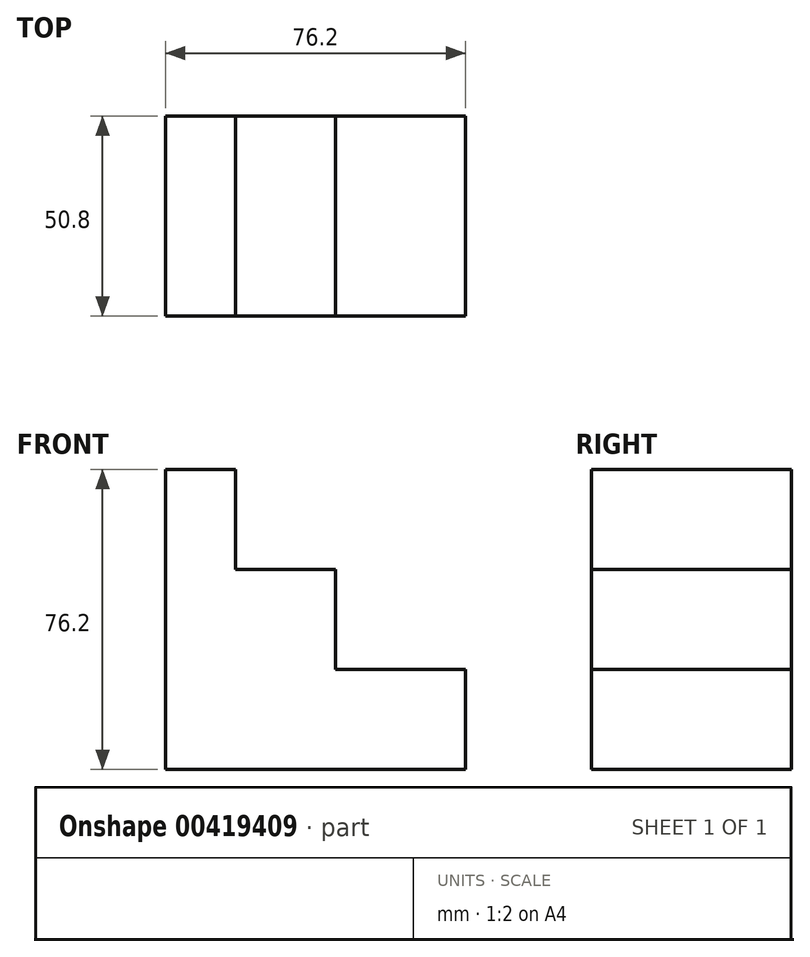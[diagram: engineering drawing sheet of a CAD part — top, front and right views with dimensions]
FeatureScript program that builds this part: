
annotation { "Feature Type Name" : "Feature", "Feature Type Description" : "" }
export const myFeature = defineFeature(function(context is Context, id is Id, definition is map)
    precondition{}
    {
        {
            var Q0;
            Q0=qCreatedBy(makeId("Front.planeOp"),FACE);
            var sketch = newSketch(context, id + "F0", { "sketchPlane" : qUnion([Q0])});
            skLineSegment(sketch, "E0", {"start": v(0, 0) * mm, "end": v(-76.2, 0) * mm});
            skLineSegment(sketch, "E1", {"start": v(-76.2, 0) * mm, "end": v(-76.2, 76.2) * mm});
            skLineSegment(sketch, "E2", {"start": v(-76.2, 76.2) * mm, "end": v(-58.4, 76.2) * mm});
            skLineSegment(sketch, "E3", {"start": v(-58.4, 76.2) * mm, "end": v(-58.4, 50.8) * mm});
            skLineSegment(sketch, "E4", {"start": v(-58.4, 50.8) * mm, "end": v(-33, 50.8) * mm});
            skLineSegment(sketch, "E5", {"start": v(-33, 50.8) * mm, "end": v(-33, 25.4) * mm});
            skLineSegment(sketch, "E6", {"start": v(-33, 25.4) * mm, "end": v(-7.6, 25.4) * mm});
            skLineSegment(sketch, "E7", {"start": v(-7.6, 25.4) * mm, "end": v(0, 25.4) * mm});
            skLineSegment(sketch, "E8", {"start": v(0, 25.4) * mm, "end": v(0, 0) * mm});
            skSolve(sketch);
        }
        {
            var Q0;
            Q0 = qSketchRegion(id + "F0", true);
            extrude(context, id + "F1", {"entities" : qUnion([Q0]), "depth" : 50.8 * mm});
        }
    });
